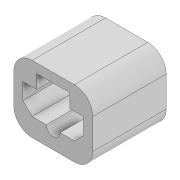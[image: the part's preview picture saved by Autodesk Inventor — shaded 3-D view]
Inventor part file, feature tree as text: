
AUTODESK INVENTOR PART (.ipt)
format: ipt  version: 2022 (Build 260153000, 153)  size: 158,720 bytes
history: native  units: mm
features: extrude x5, sketch x4, chamfer x2, projected_geometry x2, fillet x1
ambient origin geometry x8: Origin, YZ Plane, XZ Plane, XY Plane, X Axis, Y Axis, Z Axis, Center Point
bodies: Solid1 (feature_tree)
feature tree (14):
  sketch  "Sketch1"  dims[d0=0.6mm d1=4.85mm]
  extrude  "Extrusion1"  Depth=4.85mm
  extrude  "Extrusion2"  Depth=2.0mm
  extrude  "Extrusion3"  Depth=1.0mm
  extrude  "Extrusion4"  Depth=2.0mm
  chamfer  "Chamfer2"  Distance=3.0mm
  chamfer  "Chamfer3"  Distance=8.0mm
  extrude  "Extrusion5"  Depth=2.0mm
  fillet  "Fillet2"  Radius=0.5mm
  sketch  "Sketch2"  dims[d4=6.6mm d6=2.0mm]
  projected_geometry  "Projected Loop1"
  sketch  "Sketch3"  dims[d9=1.0mm d10=1.0mm]
  projected_geometry  "Projected Loop2"
  sketch  "Sketch4"  dims[d11=1.0mm d12=2.0mm d13=3.0mm d14=0.0mm d15=8.0mm d16=0.0mm d20=2.0mm d22=0.5mm d23=12.217305mm d24=7.0mm d25=0.0mm d26=1.5mm d27=1.5mm d28=1.5mm d29=1.5mm d30=5.0mm d31=0.0mm d33=1.0mm d34=2.0mm d35=45.0deg d36=1.0mm d37=2.0mm d38=45.0deg d39=1.5mm d40=10.0mm d41=0.0mm d42=2.0mm]
